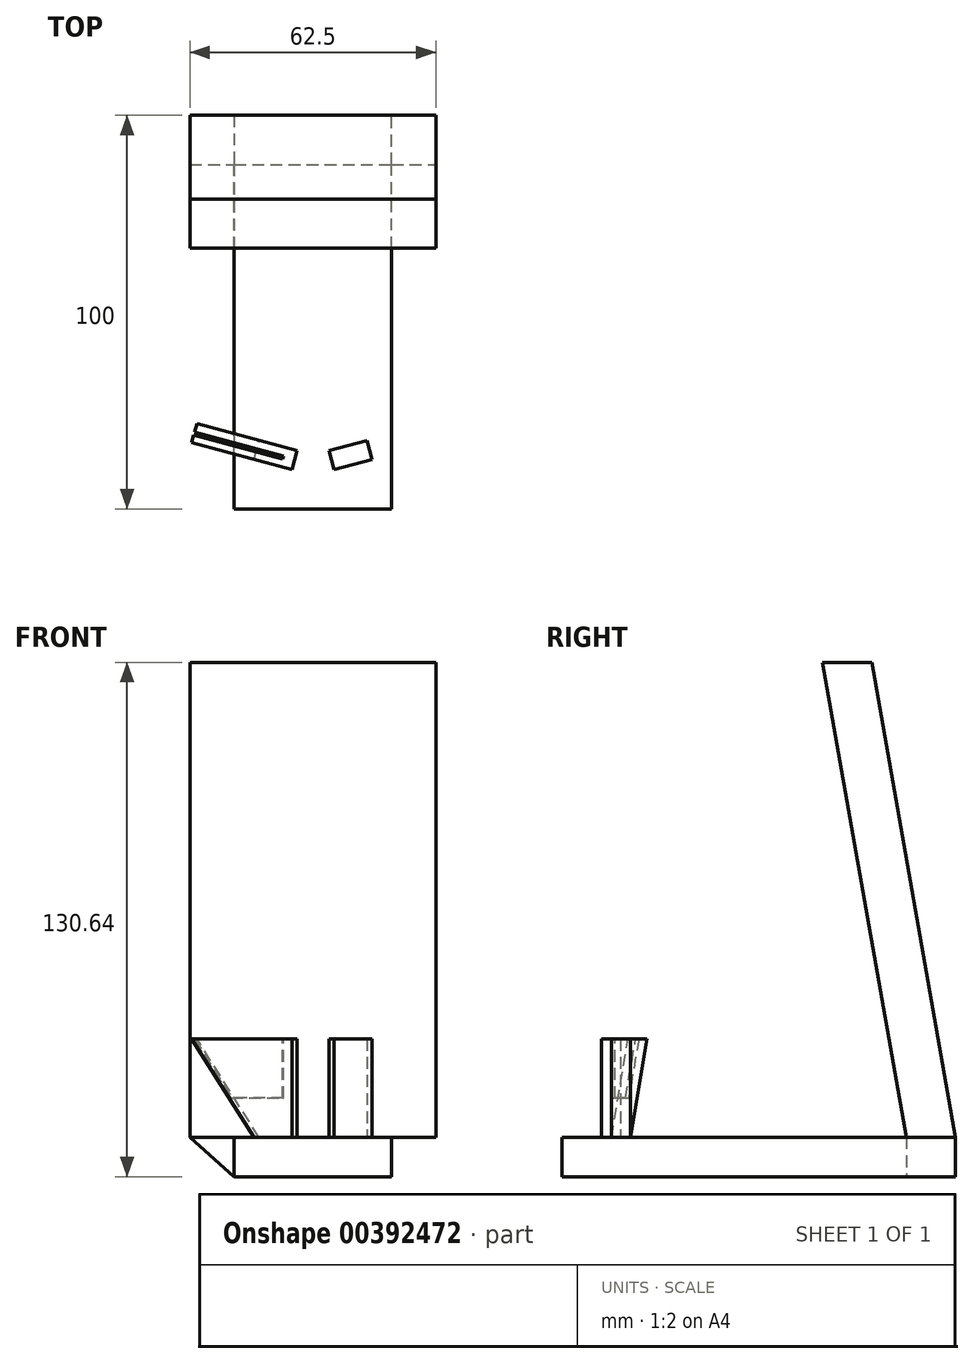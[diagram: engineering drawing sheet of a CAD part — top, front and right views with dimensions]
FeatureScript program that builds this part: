
annotation { "Feature Type Name" : "Feature", "Feature Type Description" : "" }
export const myFeature = defineFeature(function(context is Context, id is Id, definition is map)
    precondition{}
    {
        {
            var Q0;
            Q0=qCreatedBy(makeId("Right.planeOp"),FACE);
            var sketch = newSketch(context, id + "F0", { "sketchPlane" : qUnion([Q0])});
            skLineSegment(sketch, "E0", {"start": v(0, 0) * mm, "end": v(-57.05, 0) * mm});
            skLineSegment(sketch, "E1", {"start": v(-57.05, 0) * mm, "end": v(-57.05, 10) * mm});
            skLineSegment(sketch, "E2", {"start": v(-57.05, 10) * mm, "end": v(42.95, 10) * mm});
            skLineSegment(sketch, "E3", {"start": v(42.95, 10) * mm, "end": v(42.95, 0) * mm});
            skLineSegment(sketch, "E4", {"start": v(42.95, 0) * mm, "end": v(0, 0) * mm});
            skSolve(sketch);
        }
        {
            var Q0;
            Q0=makeQuery(id+"F0.imprint","IMPRINT",FACE,{"disambiguationData":[TD([[makeQuery(id+"F0.imprint","IMPRINT",EDGE,{"derivedFrom":sQuery(id+"F0.wireOp",EDGE,"E0")}),-1.0]])]});
            extrude(context, id + "F1", {"entities" : qUnion([Q0]), "depth" : 40 * mm});
        }
        {
            var Q0;
            Q0=makeQuery(id+"F1.opExtrude","CAP_FACE",FACE,{"disambiguationData":[OSD([sQuery(id+"F0.wireOp",EDGE,"E0"),sQuery(id+"F0.wireOp",EDGE,"E1"),sQuery(id+"F0.wireOp",EDGE,"E2"),sQuery(id+"F0.wireOp",EDGE,"E3"),sQuery(id+"F0.wireOp",EDGE,"E4")])],"isStart":false});
            cPlane(context, id + "F2", {"entities" : qUnion([Q0]), "cplaneType" : CPlaneType.OFFSET, "offset" : 11.25 * mm, "width" : 150 * mm, "height" : 150 * mm});
        }
        {
            var Q0;
            Q0=qCreatedBy(id+"F2.planeOp",FACE);
            var sketch = newSketch(context, id + "F3", { "sketchPlane" : qUnion([Q0])});
            skLineSegment(sketch, "E5.0", {"start": v(-57.05, 10) * mm, "end": v(42.95, 10) * mm});
            skLineSegment(sketch, "E6", {"start": v(42.95, 10) * mm, "end": v(30.45, 10) * mm});
            skLineSegment(sketch, "E7", {"start": v(30.45, 10) * mm, "end": v(9.18, 130.64) * mm});
            skLineSegment(sketch, "E8", {"start": v(9.18, 130.64) * mm, "end": v(21.68, 130.64) * mm});
            skLineSegment(sketch, "E9", {"start": v(21.68, 130.64) * mm, "end": v(42.95, 10) * mm});
            skLineSegment(sketch, "E10", {"start": v(30.45, 10) * mm, "end": v(42.95, 10) * mm});
            skSolve(sketch);
        }
        {
            var Q0;
            Q0=makeQuery(id+"F3.imprint","IMPRINT",FACE,{"disambiguationData":[TD([[makeQuery(id+"F3.imprint","IMPRINT",EDGE,{"derivedFrom":sQuery(id+"F3.wireOp",EDGE,"E7")}),-1.0]])]});
            extrude(context, id + "F4", {"entities" : qUnion([Q0]), "operationType" : NewBodyOperationType.ADD, "oppositeDirection" : true, "depth" : 62.5 * mm});
        }
        {
            var Q0;
            Q0=makeQuery(id+"F4.boolean.opBoolean","MERGE",FACE,{"derivedFrom":[makeQuery(id+"F1.opExtrude","SWEPT_FACE",FACE,{"disambiguationData":[OSD([sQuery(id+"F0.wireOp",EDGE,"E3")])]}),makeQuery(id+"F4.opExtrude","SWEPT_FACE",FACE,{"disambiguationData":[OSD([sQuery(id+"F3.wireOp",EDGE,"E9")])]})]});
            var sketch = newSketch(context, id + "F5", { "sketchPlane" : qUnion([Q0])});
            skLineSegment(sketch, "E11", {"start": v(-40, 10) * mm, "end": v(-51.25, 10) * mm});
            skLineSegment(sketch, "E12", {"start": v(-51.25, 10) * mm, "end": v(-40, 0) * mm});
            skLineSegment(sketch, "E13", {"start": v(0, 10) * mm, "end": v(0, 0) * mm});
            skLineSegment(sketch, "E14", {"start": v(0, 0) * mm, "end": v(11.25, 10) * mm});
            skLineSegment(sketch, "E15", {"start": v(11.25, 10) * mm, "end": v(0, 10) * mm});
            skSolve(sketch);
        }
        {
            var Q0;
            Q0 = qSketchRegion(id + "F5", true);
            var Q1;
            Q1=makeQuery(id+"F5.imprint","IMPRINT",FACE,{"disambiguationData":[TD([[makeQuery(id+"F5.imprint","IMPRINT",EDGE,{"derivedFrom":sQuery(id+"F5.wireOp",EDGE,"E11")}),-1.0]])]});
            extrude(context, id + "F6", {"entities" : qUnion([Q0, Q1]), "operationType" : NewBodyOperationType.ADD, "oppositeDirection" : true, "depth" : 12.5 * mm});
        }
        {
            var Q0;
            Q0=makeQuery(id+"F1.opExtrude","SWEPT_FACE",FACE,{"disambiguationData":[OSD([sQuery(id+"F0.wireOp",EDGE,"E2")])]});
            var sketch = newSketch(context, id + "F7", { "sketchPlane" : qUnion([Q0])});
            skLineSegment(sketch, "E16", {"start": v(6.3, -39.63) * mm, "end": v(15.95, -42.22) * mm});
            skLineSegment(sketch, "E17", {"start": v(15.95, -42.22) * mm, "end": v(14.66, -47.05) * mm});
            skLineSegment(sketch, "E18", {"start": v(14.66, -47.05) * mm, "end": v(5, -44.46) * mm});
            skLineSegment(sketch, "E19", {"start": v(5, -44.46) * mm, "end": v(6.3, -39.63) * mm});
            skLineSegment(sketch, "E20", {"start": v(24.05, -42.22) * mm, "end": v(25.34, -47.05) * mm});
            skLineSegment(sketch, "E21", {"start": v(25.34, -47.05) * mm, "end": v(35, -44.46) * mm});
            skLineSegment(sketch, "E22", {"start": v(35, -44.46) * mm, "end": v(33.7, -39.63) * mm});
            skLineSegment(sketch, "E23", {"start": v(33.7, -39.63) * mm, "end": v(24.05, -42.22) * mm});
            skSolve(sketch);
        }
        {
            var Q0;
            Q0=makeQuery(id+"F7.imprint","IMPRINT",FACE,{"disambiguationData":[TD([[makeQuery(id+"F7.imprint","IMPRINT",EDGE,{"derivedFrom":sQuery(id+"F7.wireOp",EDGE,"E16")}),-1.0]])]});
            var Q1;
            Q1=makeQuery(id+"F7.imprint","IMPRINT",FACE,{"disambiguationData":[TD([[makeQuery(id+"F7.imprint","IMPRINT",EDGE,{"derivedFrom":sQuery(id+"F7.wireOp",EDGE,"E20")}),1.0]])]});
            extrude(context, id + "F8", {"entities" : qUnion([Q0, Q1]), "operationType" : NewBodyOperationType.ADD, "depth" : 25 * mm});
        }
        {
            var Q0;
            Q0=makeQuery(id+"F8.opExtrude","SWEPT_FACE",FACE,{"disambiguationData":[OSD([sQuery(id+"F7.wireOp",EDGE,"E16")])]});
            var sketch = newSketch(context, id + "F9", { "sketchPlane" : qUnion([Q0])});
            skLineSegment(sketch, "E24", {"start": v(-16.34, 10) * mm, "end": v(0, 35) * mm});
            skLineSegment(sketch, "E25", {"start": v(0, 35) * mm, "end": v(-16.34, 35) * mm});
            skLineSegment(sketch, "E26", {"start": v(-16.34, 35) * mm, "end": v(-16.34, 10) * mm});
            skSolve(sketch);
        }
        {
            var Q0;
            Q0=makeQuery(id+"F9.imprint","IMPRINT",FACE,{"disambiguationData":[TD([[makeQuery(id+"F9.imprint","IMPRINT",EDGE,{"derivedFrom":sQuery(id+"F9.wireOp",EDGE,"E24")}),1.0]])]});
            extrude(context, id + "F10", {"entities" : qUnion([Q0]), "operationType" : NewBodyOperationType.ADD, "oppositeDirection" : true, "depth" : 5 * mm});
        }
        {
            var Q0;
            Q0=makeQuery(id+"F10.boolean.opBoolean","MERGE",FACE,{"derivedFrom":[makeQuery(id+"F8.opExtrude","CAP_FACE",FACE,{"disambiguationData":[OSD([sQuery(id+"F7.wireOp",EDGE,"E16"),sQuery(id+"F7.wireOp",EDGE,"E17"),sQuery(id+"F7.wireOp",EDGE,"E18"),sQuery(id+"F7.wireOp",EDGE,"E19")])],"isStart":false}),makeQuery(id+"F10.opExtrude","SWEPT_FACE",FACE,{"disambiguationData":[OSD([sQuery(id+"F9.wireOp",EDGE,"E25")])]})]});
            var sketch = newSketch(context, id + "F11", { "sketchPlane" : qUnion([Q0])});
            skLineSegment(sketch, "E27", {"start": v(12.49, -43.57) * mm, "end": v(-10.06, -37.53) * mm});
            skLineSegment(sketch, "E28", {"start": v(-10.06, -37.53) * mm, "end": v(-10.26, -38.3) * mm});
            skLineSegment(sketch, "E29", {"start": v(-10.26, -38.3) * mm, "end": v(12.28, -44.34) * mm});
            skLineSegment(sketch, "E30", {"start": v(12.28, -44.34) * mm, "end": v(12.49, -43.57) * mm});
            skSolve(sketch);
        }
        {
            var Q0;
            Q0=makeQuery(id+"F11.imprint","IMPRINT",FACE,{"disambiguationData":[TD([[makeQuery(id+"F11.imprint","IMPRINT",EDGE,{"derivedFrom":sQuery(id+"F11.wireOp",EDGE,"E27")}),1.0]])]});
            extrude(context, id + "F12", {"entities" : qUnion([Q0]), "operationType" : NewBodyOperationType.REMOVE, "oppositeDirection" : true, "depth" : 15 * mm});
        }
        {
            var Q0;
            Q0=makeQuery(id+"F1.opExtrude","CAP_FACE",FACE,{"disambiguationData":[OSD([sQuery(id+"F0.wireOp",EDGE,"E0"),sQuery(id+"F0.wireOp",EDGE,"E1"),sQuery(id+"F0.wireOp",EDGE,"E2"),sQuery(id+"F0.wireOp",EDGE,"E3"),sQuery(id+"F0.wireOp",EDGE,"E4")])],"isStart":true});
            cPlane(context, id + "F13", {"entities" : qUnion([Q0]), "cplaneType" : CPlaneType.OFFSET, "offset" : 20 * mm, "oppositeDirection" : true, "width" : 150 * mm, "height" : 150 * mm});
        }
    });
